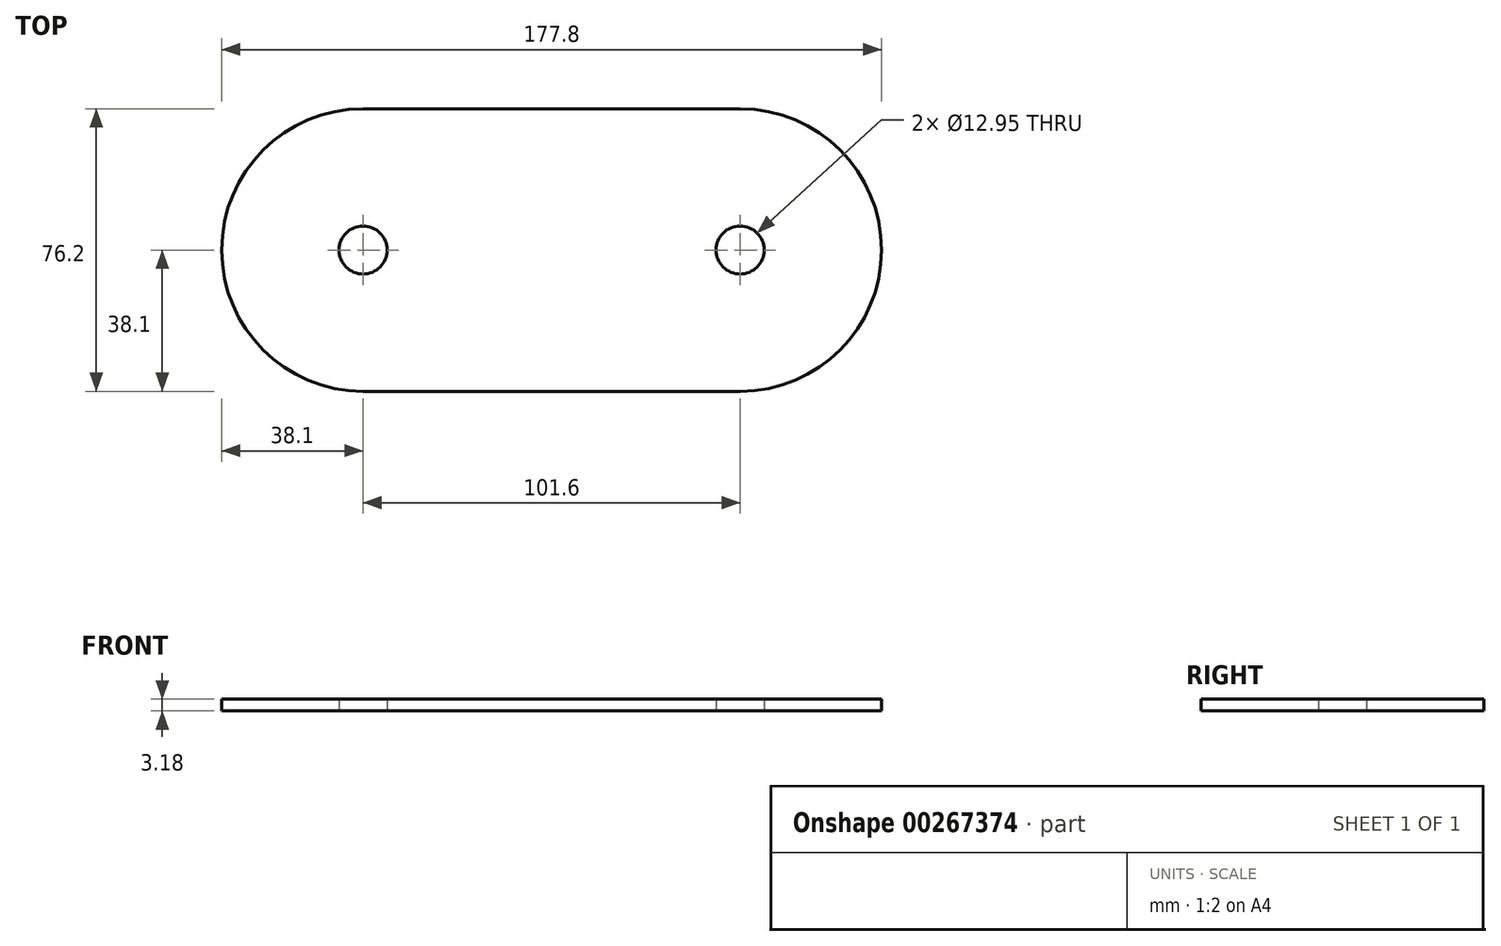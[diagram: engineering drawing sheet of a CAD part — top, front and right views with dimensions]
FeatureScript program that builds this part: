
annotation { "Feature Type Name" : "Feature", "Feature Type Description" : "" }
export const myFeature = defineFeature(function(context is Context, id is Id, definition is map)
    precondition{}
    {
        {
            var Q0;
            Q0=qCreatedBy(makeId("Top.planeOp"),FACE);
            var sketch = newSketch(context, id + "F0", { "sketchPlane" : qUnion([Q0])});
            skLineSegment(sketch, "E0.bottom", {"start": v(-38.1, 38.1) * mm, "end": v(63.5, 38.1) * mm});
            skLineSegment(sketch, "E0.top", {"start": v(-38.1, -38.1) * mm, "end": v(63.5, -38.1) * mm});
            skLineSegment(sketch, "E0.left", {"start": v(-38.1, 38.1) * mm, "end": v(-38.1, -38.1) * mm});
            skLineSegment(sketch, "E0.right", {"start": v(63.5, 38.1) * mm, "end": v(63.5, -38.1) * mm});
            skArc(sketch, "E1", {"start": v(-38.1, 38.1) * mm, "mid": v(-76.2, 0) * mm, "end": v(-38.1, -38.1) * mm});
            skArc(sketch, "E2", {"start": v(63.5, -38.1) * mm, "mid": v(101.6, 0) * mm, "end": v(63.5, 38.1) * mm});
            skCircle(sketch, "E3", {"center": v(63.5, 0) * mm, "radius": 6.48 * mm});
            skCircle(sketch, "E4", {"center": v(-38.1, 0) * mm, "radius": 6.48 * mm});
            skSolve(sketch);
        }
        {
            var Q0;
            Q0 = qSketchRegion(id + "F0", true);
            extrude(context, id + "F1", {"entities" : qUnion([Q0]), "depth" : 3.17 * mm});
        }
    });
